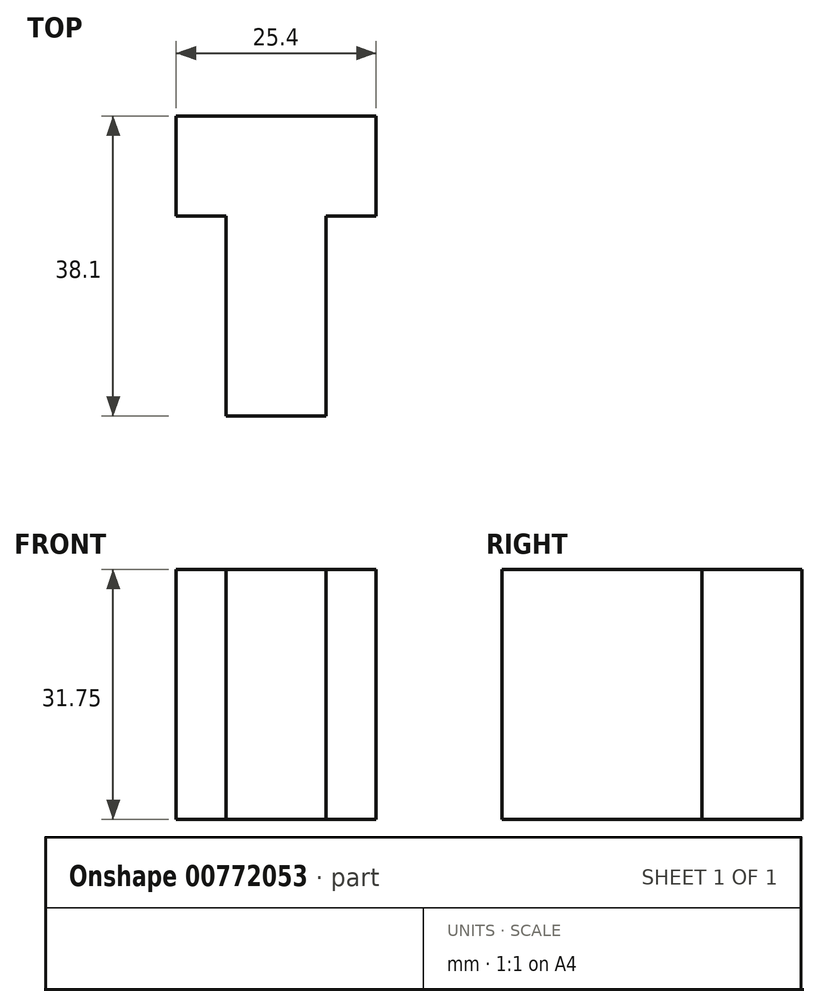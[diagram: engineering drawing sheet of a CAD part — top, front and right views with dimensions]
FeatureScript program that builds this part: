
annotation { "Feature Type Name" : "Feature", "Feature Type Description" : "" }
export const myFeature = defineFeature(function(context is Context, id is Id, definition is map)
    precondition{}
    {
        {
            var Q0;
            Q0=qCreatedBy(makeId("Top.planeOp"),FACE);
            var sketch = newSketch(context, id + "F0", { "sketchPlane" : qUnion([Q0])});
            skLineSegment(sketch, "E0", {"start": v(0, 0) * mm, "end": v(0, -12.7) * mm});
            skLineSegment(sketch, "E1", {"start": v(0, -12.7) * mm, "end": v(6.35, -12.7) * mm});
            skLineSegment(sketch, "E2", {"start": v(6.35, -12.7) * mm, "end": v(6.35, -38.1) * mm});
            skLineSegment(sketch, "E3", {"start": v(6.35, -38.1) * mm, "end": v(19.05, -38.1) * mm});
            skLineSegment(sketch, "E4", {"start": v(19.05, -38.1) * mm, "end": v(19.05, -12.7) * mm});
            skLineSegment(sketch, "E5", {"start": v(19.05, -12.7) * mm, "end": v(25.4, -12.7) * mm});
            skLineSegment(sketch, "E6", {"start": v(25.4, -12.7) * mm, "end": v(25.4, 0) * mm});
            skLineSegment(sketch, "E7", {"start": v(25.4, 0) * mm, "end": v(0, 0) * mm});
            skSolve(sketch);
        }
        {
            var Q0;
            Q0 = qSketchRegion(id + "F0", true);
            extrude(context, id + "F1", {"entities" : qUnion([Q0]), "depth" : 31.75 * mm, "offsetDistance" : 25.4 * mm});
        }
    });
